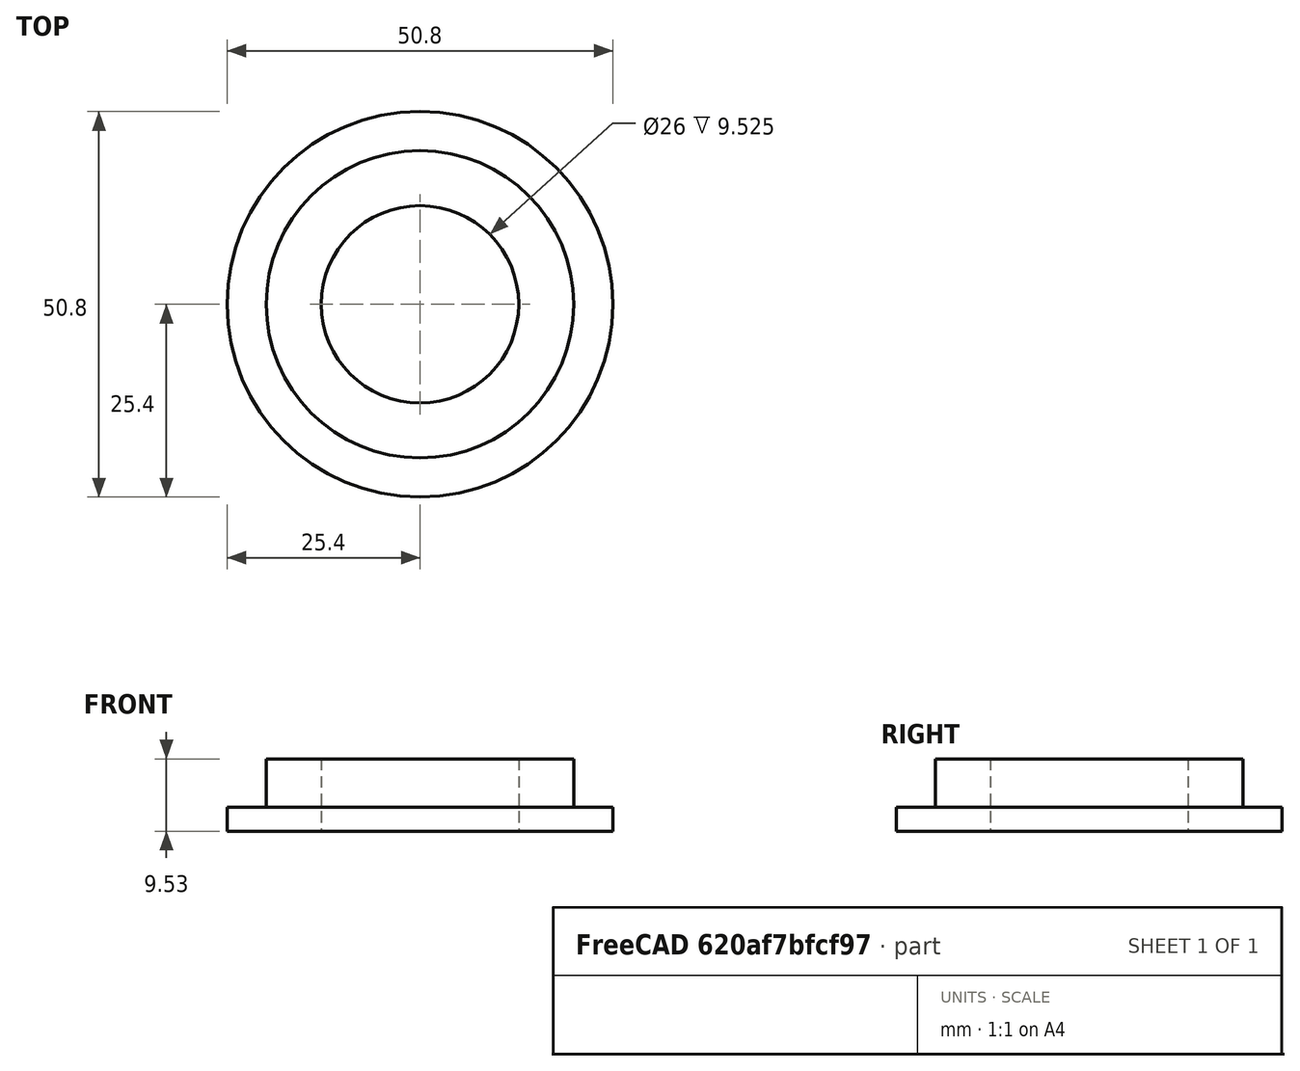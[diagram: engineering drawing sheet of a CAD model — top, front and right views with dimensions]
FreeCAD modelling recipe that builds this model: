
FCSTD DOCUMENT  (FreeCAD 1.0R39319 (Git))
Label: post_bushing
License: All rights reserved
LicenseURL: https://en.wikipedia.org/wiki/All_rights_reserved
objects: Sketcher::SketchObject×1, PartDesign::Revolution×1, PartDesign::Body×1
note: 6 computed .brp shape members not serialized (recipe doc carries the construction recipe); baked Part::Feature solids carry a one-line shape summary decoded from their .brp

FEATURE [Sketcher::SketchObject] Sketch
  ArcFitTolerance = 1e-06
  AttachmentSupport = -> [XZ_Plane]
  FullyConstrained = false
  MakeInternals = false
  MapMode = 5
  Placement = pos=(0,0,0) rot=(1,0,0;1.5708rad)
  sketch-geometry (7):
    g0: LineSegment StartX=13 StartY=0 StartZ=0 EndX=25.4 EndY=0 EndZ=0
    g1: LineSegment StartX=25.4 StartY=0 StartZ=0 EndX=25.4 EndY=3.175 EndZ=0
    g2: LineSegment StartX=25.4 StartY=3.175 StartZ=0 EndX=20.25 EndY=3.175 EndZ=0
    g3: LineSegment StartX=20.25 StartY=3.175 StartZ=0 EndX=20.25 EndY=9.525 EndZ=0
    g4: LineSegment StartX=20.25 StartY=9.525 StartZ=0 EndX=13 EndY=9.525 EndZ=0
    g5: LineSegment StartX=13 StartY=9.525 StartZ=0 EndX=13 EndY=0 EndZ=0
    g6: LineSegment [constr] StartX=0 StartY=0 StartZ=0 EndX=0 EndY=14.8796 EndZ=0
  constraints (20):
    c: PointOnObject(g0,g-1)
    c: PointOnObject(g0,g-1)
    c: Coincident(g1,g0)
    c: Vertical(g1)
    c: Coincident(g2,g1)
    c: Horizontal(g2)
    c: Coincident(g3,g2)
    c: Vertical(g3)
    c: Coincident(g4,g3)
    c: Horizontal(g4)
    c: Coincident(g5,g4)
    c: Vertical(g5)
    c: Coincident(g0,g5)
    c: Distance(g-1,g1) = 25.4
    c: DistanceY(g3,g3) = 6.35
    c: Distance(g-1,g5) = 13
    c: DistanceY(g1,g1) = 3.175
    c: Distance(g-1,g3) = 20.25
    c: Coincident(g6,g-1)
    c: PointOnObject(g6,g-2)
FEATURE [PartDesign::Revolution] Revolution
  Angle = 360
  Angle2 = 60
  Axis = (0,2e-16,1)
  Base = (0,0,0)
  Placement = pos=(0,0,0) rot=(1,0,0;1.5708rad)
  Profile = -> Sketch
  ReferenceAxis = -> Sketch [V_Axis]
  Refine = true
  Reversed = true
  Suppressed = false
  Type = 0
FEATURE [PartDesign::Body] Body
  AllowCompound = false
  Group = -> [Sketch,Revolution]
  Origin = -> Origin
  Tip = -> Revolution
